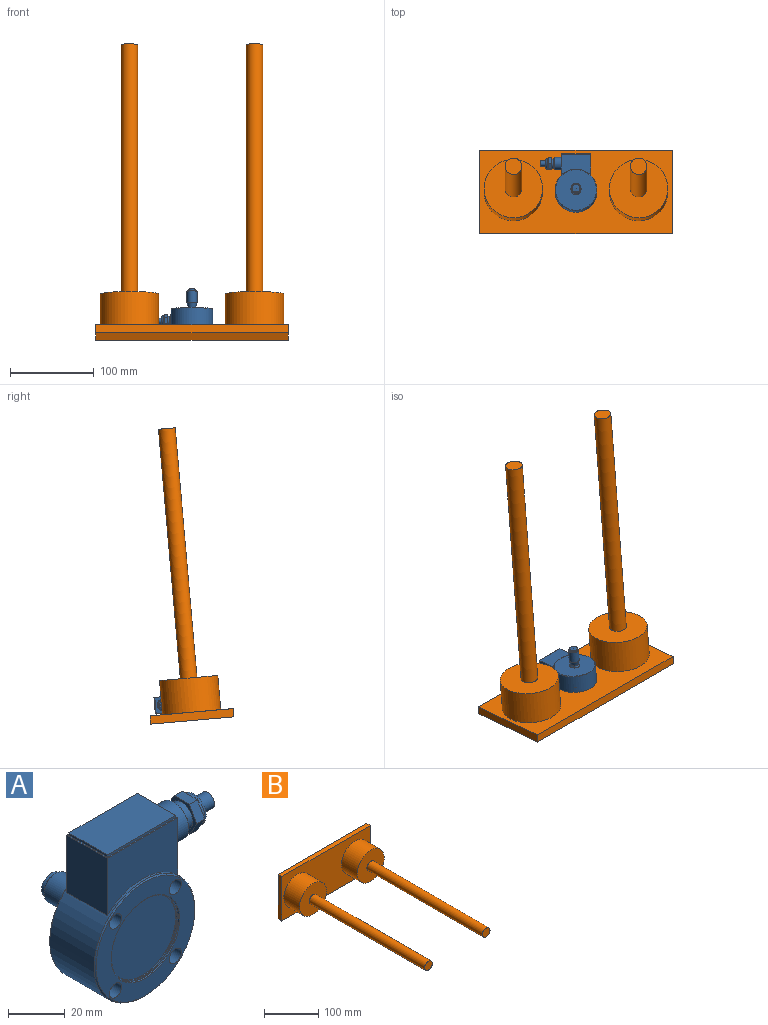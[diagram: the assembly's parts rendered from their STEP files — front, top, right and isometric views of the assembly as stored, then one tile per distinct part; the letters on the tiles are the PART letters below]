
ASSEMBLY  parts=2 mates=1
PART A: 73 faces, bbox 67.5x47x68.5 mm
  f0: cylinder r=7.5mm len=4mm, axis (1,0,0), area 0.1mm2, adj f5,f59,f71,f72
  f1: cylinder r=7.5mm len=4mm, axis (1,0,0), area 0.1mm2, adj f6,f59,f69,f70
  f2: cylinder r=7.5mm len=4mm, axis (1,0,0), area 0.1mm2, adj f7,f59,f68,f69
  f3: cylinder r=7.5mm len=4mm, axis (1,0,0), area 0.1mm2, adj f8,f59,f67,f68
  f4: cylinder r=7.5mm len=4mm, axis (1,0,0), area 0.1mm2, adj f9,f59,f67,f72
  f5: plane 5.63x3.25mm, normal (1,0,0), area 2.3mm2, adj f0,f62,f71,f72
  f6: plane 5.63x3.25mm, normal (1,0,0), area 2.3mm2, adj f1,f62,f69,f70
  f7: plane 5.63x3.25mm, normal (1,0,0), area 2.3mm2, adj f2,f62,f68,f69
  f8: plane 6.5x1.87mm, normal (1,0,0), area 2.3mm2, adj f3,f62,f67,f68
  f9: plane 5.63x3.25mm, normal (1,0,0), area 2.3mm2, adj f4,f62,f67,f72
  f10: cylinder r=25mm len=50mm, axis (0,-1,0), area 2680.4mm2, adj f14,f15,f27,f28,f29,f31
  f11: cone r=6mm half-angle=15deg, axis (0,1,0), area 194.5mm2, adj f12,f26
  f12: torus R=5.92mm, axis (0,-1,0), area 84.4mm2, adj f11,f13
  f13: plane 49x49mm, normal (0,1,0), area 1775.7mm2, adj f12,f14
  f14: cone r=24.5mm half-angle=45deg, axis (0,-1,0), area 110mm2, adj f10,f13
  f15: cone r=25mm half-angle=45deg, axis (0,1,0), area 110mm2, adj f10,f16
  f16: plane 49x49mm, normal (0,-1,0), area 864.7mm2, adj f15,f17,f35,f39,f43,f47
  f17: torus R=17mm, axis (0,-1,0), area 83.1mm2, adj f16,f18
  f18: cylinder r=17mm len=34mm, axis (0,-1,0), area 53.4mm2, adj f17,f19
  f19: plane 34x34mm, normal (0,-1,0), area 52.6mm2, adj f18,f20
  f20: cylinder r=16.5mm len=33mm, axis (0,-1,0), area 51.8mm2, adj f19,f21
  f21: plane 33x33mm, normal (0,-1,0), area 855.3mm2, adj f20
  f22: sphere r=60mm, area 71mm2, adj f23
  f23: cylinder r=4.75mm len=9.5mm, axis (0,-1,0), area 42.1mm2, adj f22,f24
  f24: plane 9.85x9.85mm, normal (0,1,0), area 5.4mm2, adj f23,f25
  f25: cone r=4.93mm half-angle=45deg, axis (0,-1,0), area 52.1mm2, adj f24,f26
  f26: cylinder r=6mm len=13.73mm, axis (0,-1,0), area 517.5mm2, adj f11,f25
  f27: plane 24.65x20mm, normal (-1,0,0), area 492.9mm2, adj f10,f29,f30,f31
  f28: plane 24.65x20mm, normal (1,0,0), area 316.2mm2, adj f10,f29,f30,f31,f53
  f29: plane 35x24.65mm, normal (0,-1,0), area 690.4mm2, adj f10,f27,f28,f30
  f30: plane 35x20mm, normal (0,0,1), area 54mm2, adj f27,f28,f29,f31,f48,f49,f50,f51
  f31: plane 35x24.65mm, normal (0,1,0), area 690.4mm2, adj f10,f27,f28,f30
  f32: cone r=0mm half-angle=60deg, axis (0,-1,0), area 15.5mm2, adj f33
  f33: cylinder r=2.07mm len=9.5mm, axis (0,-1,0), area 123.4mm2, adj f32,f34
  f34: plane 6x6mm, normal (0,-1,0), area 14.9mm2, adj f33,f35
  f35: cylinder r=3mm len=6.5mm, axis (0,-1,0), area 122.5mm2, adj f16,f34
  f36: cone r=0mm half-angle=60deg, axis (0,-1,0), area 15.5mm2, adj f37
  f37: cylinder r=2.07mm len=9.5mm, axis (0,-1,0), area 123.4mm2, adj f36,f38
  f38: plane 6x6mm, normal (0,-1,0), area 14.9mm2, adj f37,f39
  f39: cylinder r=3mm len=6.5mm, axis (0,-1,0), area 122.5mm2, adj f16,f38
  f40: cone r=0mm half-angle=60deg, axis (0,-1,0), area 15.5mm2, adj f41
  f41: cylinder r=2.07mm len=9.5mm, axis (0,-1,0), area 123.4mm2, adj f40,f42
  f42: plane 6x6mm, normal (0,-1,0), area 14.9mm2, adj f41,f43
  f43: cylinder r=3mm len=6.5mm, axis (0,-1,0), area 122.5mm2, adj f16,f42
  f44: cone r=0mm half-angle=60deg, axis (0,-1,0), area 15.5mm2, adj f45
  f45: cylinder r=2.07mm len=9.5mm, axis (0,-1,0), area 123.4mm2, adj f44,f46
  f46: plane 6x6mm, normal (0,-1,0), area 14.9mm2, adj f45,f47
  f47: cylinder r=3mm len=6.5mm, axis (0,-1,0), area 122.5mm2, adj f16,f46
  f48: plane 34x1mm, normal (0,1,0), area 34mm2, adj f30,f49,f51,f52
  f49: plane 19x1mm, normal (-1,0,0), area 19mm2, adj f30,f48,f50,f52
  f50: plane 34x1mm, normal (0,-1,0), area 34mm2, adj f30,f49,f51,f52
  f51: plane 19x1mm, normal (1,0,0), area 19mm2, adj f30,f48,f50,f52
  f52: plane 34x19mm, normal (0,0,1), area 646mm2, adj f48,f49,f50,f51
  f53: cylinder r=7.5mm len=15mm, axis (1,0,0), area 377mm2, adj f28,f54
  f54: plane 15x15mm, normal (1,0,0), area 63.6mm2, adj f53,f55
  f55: cylinder r=6mm len=12mm, axis (1,0,0), area 45.2mm2, adj f54,f56
  f56: cone r=6mm half-angle=45deg, axis (-1,0,0), area 15.6mm2, adj f55,f57
  f57: plane 11.4x11.4mm, normal (1,0,0), area 7mm2, adj f56,f58
  f58: cylinder r=5.5mm len=11mm, axis (1,0,0), area 86.4mm2, adj f57,f59
  f59: plane 15x13mm, normal (-1,0,0), area 51.3mm2, adj f0,f1,f2,f3,f4,f58,f60,f67
  f60: cylinder r=7.5mm len=4mm, axis (1,0,0), area 0.1mm2, adj f59,f61,f70,f71
  f61: plane 6.5x1.87mm, normal (1,0,0), area 2.3mm2, adj f60,f62,f70,f71
  f62: cylinder r=6.5mm len=13mm, axis (1,0,0), area 40.8mm2, adj f5,f6,f7,f8,f9,f61,f63
  f63: torus R=5mm, axis (1,0,0), area 88.2mm2, adj f62,f64
  f64: plane 10x10mm, normal (1,0,0), area 45.4mm2, adj f63,f65
  f65: cylinder r=3.25mm len=6.5mm, axis (1,0,0), area 132.7mm2, adj f64,f66
  f66: plane 6.5x6.5mm, normal (1,0,0), area 33.2mm2, adj f65
  f67: plane 6.48x4mm, normal (0,-0.87,0.5), area 29.9mm2, adj f3,f4,f8,f9,f59
  f68: plane 6.48x4mm, normal (0,-0.87,-0.5), area 29.9mm2, adj f2,f3,f7,f8,f59
  f69: plane 7.48x4mm, normal (0,0,-1), area 29.9mm2, adj f1,f2,f6,f7,f59
  f70: plane 6.48x4mm, normal (0,0.87,-0.5), area 29.9mm2, adj f1,f6,f59,f60,f61
  f71: plane 6.48x4mm, normal (0,0.87,0.5), area 29.9mm2, adj f0,f5,f59,f60,f61
  f72: plane 7.48x4mm, normal (0,0,1), area 29.9mm2, adj f0,f4,f5,f9,f59
PART B: 14 faces, bbox 230x351x100 mm
  f0: plane 100x10mm, normal (-1,0,0), area 1000mm2, adj f1,f3,f4,f5
  f1: plane 230x10mm, normal (0,0,-1), area 2300mm2, adj f0,f2,f4,f5
  f2: plane 100x10mm, normal (1,0,0), area 1000mm2, adj f1,f3,f4,f5
  f3: plane 230x10mm, normal (0,0,1), area 2300mm2, adj f0,f2,f4,f5
  f4: plane 230x100mm, normal (0,-1,0), area 15303.1mm2, adj f0,f1,f2,f3,f6,f8
  f5: plane 230x100mm, normal (0,1,0), area 23000mm2, adj f0,f1,f2,f3
  f6: cylinder r=35mm len=70mm, axis (0,1,0), area 9016.4mm2, adj f4,f7
  f7: plane 70x70mm, normal (0,-1,0), area 3534.3mm2, adj f6,f10
  f8: cylinder r=35mm len=70mm, axis (0,1,0), area 9016.4mm2, adj f4,f9
  f9: plane 70x70mm, normal (0,-1,0), area 3534.3mm2, adj f8,f12
  f10: cylinder r=10mm len=300mm, axis (0,1,0), area 18849.6mm2, adj f7,f11
  f11: plane 20x20mm, normal (0,-1,0), area 314.2mm2, adj f10
  f12: cylinder r=10mm len=300mm, axis (0,1,0), area 18849.6mm2, adj f9,f13
  f13: plane 20x20mm, normal (0,-1,0), area 314.2mm2, adj f12
PLACE A rot(axis=(0,0.74,0.68),180deg) t=(-67.56,92.91,-34.72)mm
PLACE B rot(axis=(-1,0,0),95deg) t=(-67.56,92.04,-44.68)mm
MATE parallel A.f11 <-> B.f4  axis (0,-0.09,-1) through (-67.56,92.91,-34.72)mm
